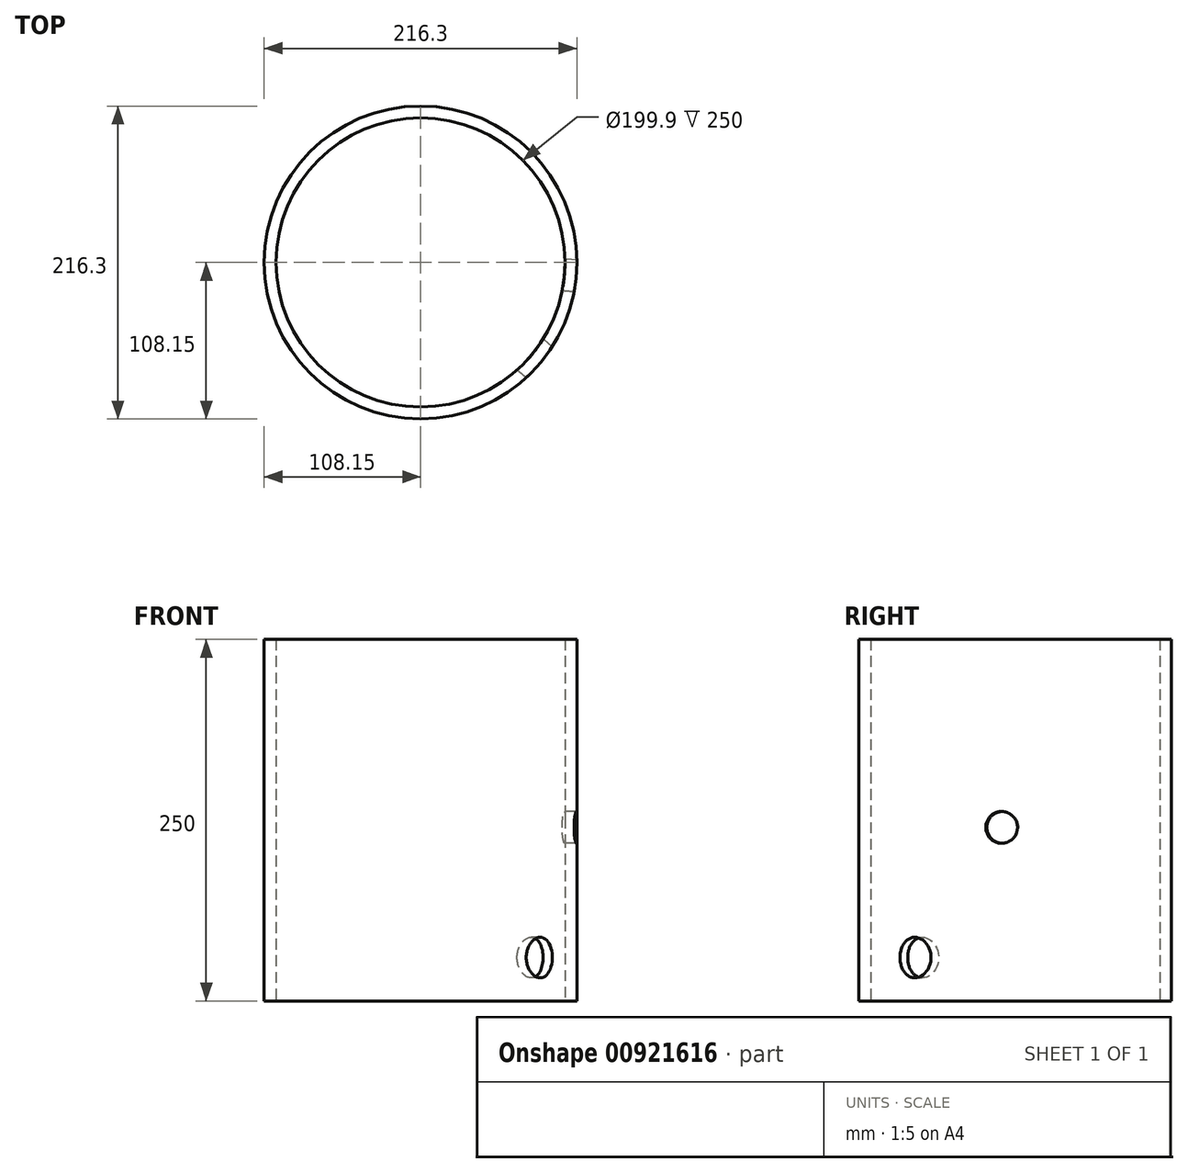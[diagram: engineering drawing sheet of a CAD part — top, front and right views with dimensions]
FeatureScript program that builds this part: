
annotation { "Feature Type Name" : "Feature", "Feature Type Description" : "" }
export const myFeature = defineFeature(function(context is Context, id is Id, definition is map)
    precondition{}
    {
        {
            var Q0;
            Q0=qCreatedBy(makeId("Top.planeOp"),FACE);
            var sketch = newSketch(context, id + "F0", { "sketchPlane" : qUnion([Q0])});
            skCircle(sketch, "E0", {"center": v(0, 0) * mm, "radius": 108.15 * mm});
            skCircle(sketch, "E1.0", {"center": v(0, 0) * mm, "radius": 99.95 * mm});
            skSolve(sketch);
        }
        {
            var Q0;
            Q0 = qSketchRegion(id + "F0", true);
            extrude(context, id + "F1", {"entities" : qUnion([Q0]), "depth" : 250 * mm, "offsetDistance" : 25 * mm});
        }
        {
            var Q0;
            Q0=makeQuery(id+"F1.opExtrude","SWEPT_FACE",FACE,{"disambiguationData":[OSD([sQuery(id+"F0.wireOp",EDGE,"E0")])]});
            cPlane(context, id + "F2", {"entities" : qUnion([Q0]), "cplaneType" : CPlaneType.LINE_ANGLE, "offset" : 25 * mm, "angle" : 40 * degree, "width" : 150 * mm, "height" : 150 * mm});
        }
        {
            var Q0;
            Q0=qCreatedBy(id+"F2.planeOp",FACE);
            var sketch = newSketch(context, id + "F3", { "sketchPlane" : qUnion([Q0])});
            skCircle(sketch, "E2", {"center": v(0, 30) * mm, "radius": 14 * mm});
            skSolve(sketch);
        }
        {
            var Q0;
            Q0=makeQuery(id+"F3.imprint","IMPRINT",FACE,{"disambiguationData":[TD([[makeQuery(id+"F3.imprint","IMPRINT",EDGE,{"derivedFrom":sQuery(id+"F3.wireOp",EDGE,"E2")}),1.0]])]});
            var Q1;
            Q1=makeQuery(id+"F1.opExtrude","SWEPT_FACE",FACE,{"disambiguationData":[OSD([sQuery(id+"F0.wireOp",EDGE,"E0")])]});
            var Q2;
            Q2=makeQuery(id+"F1.opExtrude","SWEPT_BODY",BODY,{"disambiguationData":[OSD([sQuery(id+"F0.wireOp",EDGE,"E0"),sQuery(id+"F0.wireOp",EDGE,"E1.0")])]});
            extrude(context, id + "F4", {"entities" : qUnion([Q0]), "operationType" : NewBodyOperationType.REMOVE, "endBound" : BoundingType.UP_TO_SURFACE, "oppositeDirection" : true, "depth" : 25 * mm, "endBoundEntityFace" : qUnion([Q1]), "endBoundEntityBody" : qUnion([Q2]), "offsetDistance" : 25 * mm});
        }
        {
            var Q0;
            Q0=qCreatedBy(makeId("Right.planeOp"),FACE);
            var Q1;
            Q1=makeQuery(id+"F1.opExtrude","CAP_EDGE",EDGE,{"disambiguationData":[OSD([sQuery(id+"F0.wireOp",EDGE,"E0")])],"isStart":false});
            cPlane(context, id + "F5", {"entities" : qUnion([Q0, Q1]), "cplaneType" : CPlaneType.LINE_ANGLE, "offset" : 25 * mm, "angle" : 5 * degree, "oppositeDirection" : true, "width" : 150 * mm, "height" : 150 * mm});
        }
        {
            var Q0;
            Q0=qCreatedBy(id+"F5.planeOp",FACE);
            var sketch = newSketch(context, id + "F6", { "sketchPlane" : qUnion([Q0])});
            skCircle(sketch, "E3", {"center": v(0, 120) * mm, "radius": 11 * mm});
            skSolve(sketch);
        }
        {
            var Q0;
            Q0=makeQuery(id+"F6.imprint","IMPRINT",FACE,{"disambiguationData":[TD([[makeQuery(id+"F6.imprint","IMPRINT",EDGE,{"derivedFrom":sQuery(id+"F6.wireOp",EDGE,"E3")}),1.0]])]});
            var Q1;
            Q1=makeQuery(id+"F1.opExtrude","SWEPT_FACE",FACE,{"disambiguationData":[OSD([sQuery(id+"F0.wireOp",EDGE,"E0")])]});
            extrude(context, id + "F7", {"entities" : qUnion([Q0]), "operationType" : NewBodyOperationType.REMOVE, "endBound" : BoundingType.UP_TO_SURFACE, "oppositeDirection" : true, "depth" : 25 * mm, "endBoundEntityFace" : qUnion([Q1]), "offsetDistance" : 25 * mm});
        }
    });
